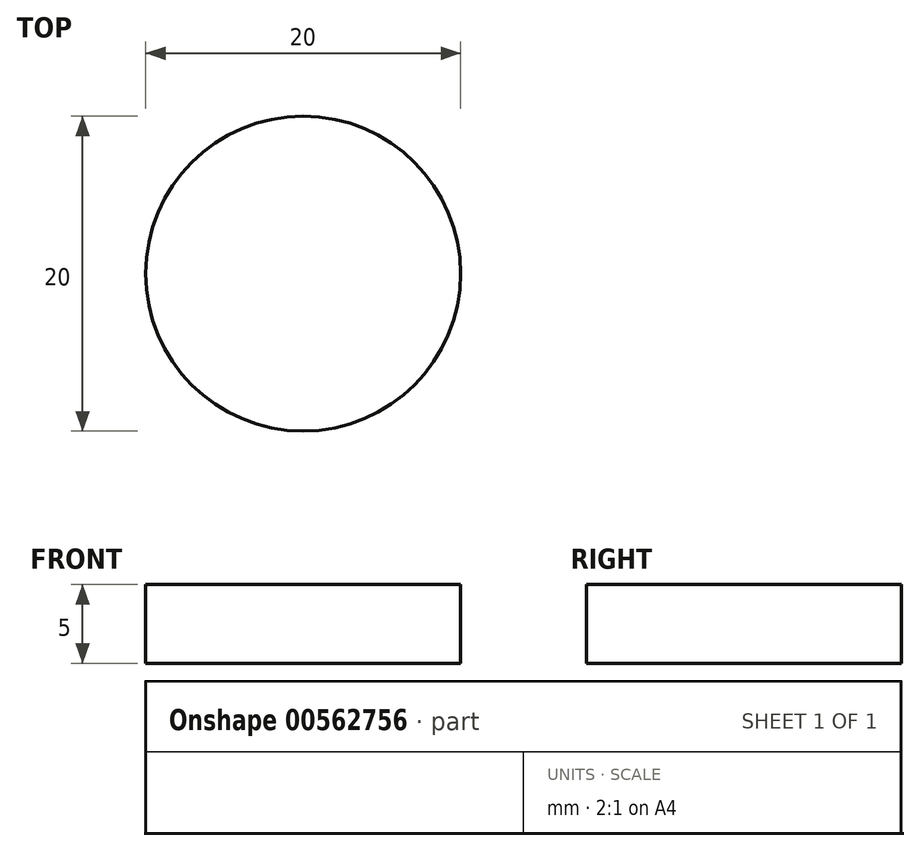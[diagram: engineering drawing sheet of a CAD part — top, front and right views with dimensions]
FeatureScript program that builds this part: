
annotation { "Feature Type Name" : "Feature", "Feature Type Description" : "" }
export const myFeature = defineFeature(function(context is Context, id is Id, definition is map)
    precondition{}
    {
        {
            var Q0;
            Q0=qCreatedBy(makeId("Top.planeOp"),FACE);
            var sketch = newSketch(context, id + "F0", { "sketchPlane" : qUnion([Q0])});
            skCircle(sketch, "E0", {"center": v(0, 0) * mm, "radius": 10 * mm});
            skSolve(sketch);
        }
        {
            var Q0;
            Q0 = qSketchRegion(id + "F0", true);
            extrude(context, id + "F1", {"entities" : qUnion([Q0]), "depth" : 5 * mm, "offsetDistance" : 25 * mm});
        }
    });
